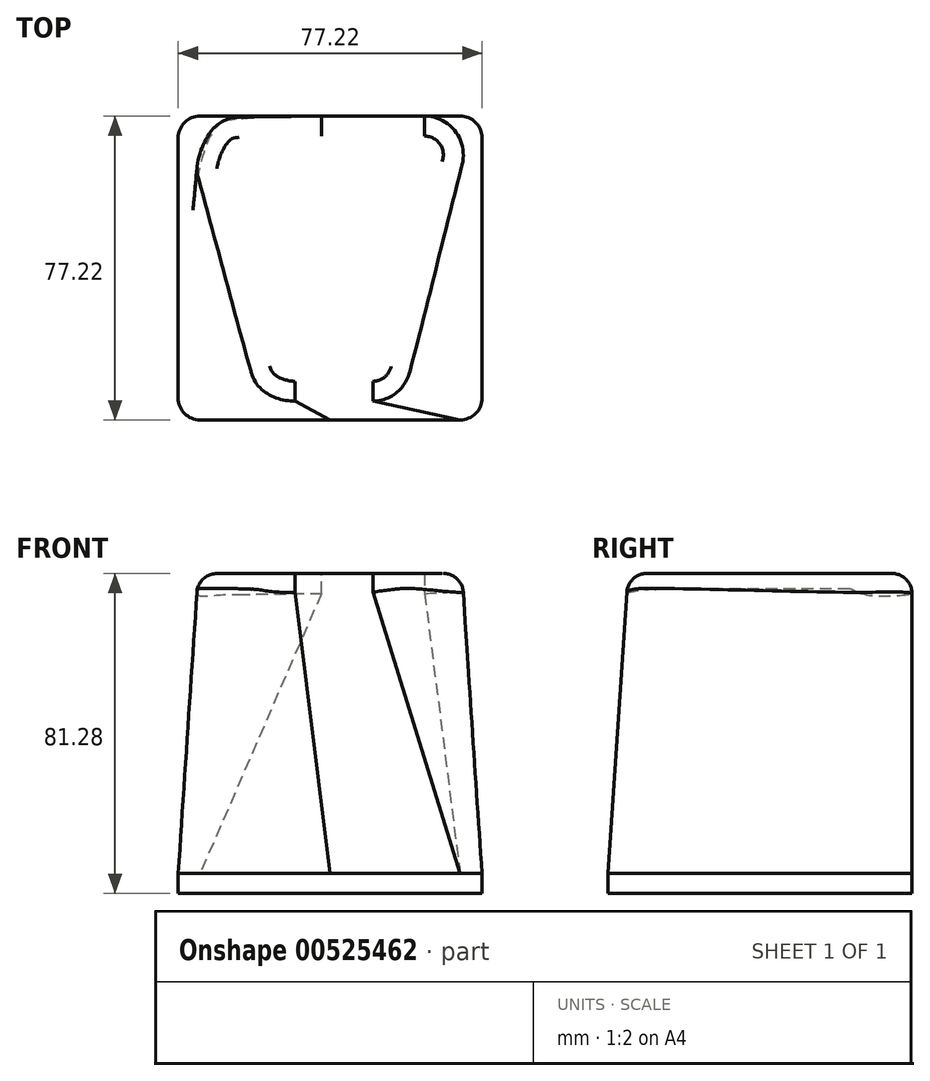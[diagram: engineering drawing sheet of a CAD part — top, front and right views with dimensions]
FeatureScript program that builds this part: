
annotation { "Feature Type Name" : "Feature", "Feature Type Description" : "" }
export const myFeature = defineFeature(function(context is Context, id is Id, definition is map)
    precondition{}
    {
        {
            var Q0;
            Q0=qCreatedBy(makeId("Top.planeOp"),FACE);
            var sketch = newSketch(context, id + "F0", { "sketchPlane" : qUnion([Q0])});
            skLineSegment(sketch, "E0.bottom", {"start": v(33.02, 38.1) * mm, "end": v(-33.02, 38.1) * mm, "construction": true});
            skLineSegment(sketch, "E0.top", {"start": v(33.02, -38.1) * mm, "end": v(-33.02, -38.1) * mm, "construction": true});
            skLineSegment(sketch, "E0.left", {"start": v(38.1, 33.02) * mm, "end": v(38.1, -33.02) * mm, "construction": true});
            skLineSegment(sketch, "E0.right", {"start": v(-38.1, 33.02) * mm, "end": v(-38.1, -33.02) * mm, "construction": true});
            skPoint(sketch, "E0.middle", {"position": v(0, 0) * mm});
            skPoint(sketch, "E1.visualSharp", {"position": v(-38.1, 38.1) * mm});
            skArc(sketch, "E1.filletArc", {"start": v(-33.02, 38.1) * mm, "mid": v(-36.61, 36.61) * mm, "end": v(-38.1, 33.02) * mm, "construction": true});
            skPoint(sketch, "E2.visualSharp", {"position": v(38.1, 38.1) * mm});
            skArc(sketch, "E2.filletArc", {"start": v(38.1, 33.02) * mm, "mid": v(36.61, 36.61) * mm, "end": v(33.02, 38.1) * mm, "construction": true});
            skPoint(sketch, "E3.visualSharp", {"position": v(38.1, -38.1) * mm});
            skArc(sketch, "E3.filletArc", {"start": v(33.02, -38.1) * mm, "mid": v(36.61, -36.61) * mm, "end": v(38.1, -33.02) * mm, "construction": true});
            skPoint(sketch, "E4.visualSharp", {"position": v(-38.1, -38.1) * mm});
            skArc(sketch, "E4.filletArc", {"start": v(-38.1, -33.02) * mm, "mid": v(-36.61, -36.61) * mm, "end": v(-33.02, -38.1) * mm, "construction": true});
            skLineSegment(sketch, "E5.0", {"start": v(-38.6, 33.02) * mm, "end": v(-38.6, -33.02) * mm});
            skArc(sketch, "E5.1", {"start": v(-33.02, 38.6) * mm, "mid": v(-36.97, 36.97) * mm, "end": v(-38.6, 33.02) * mm});
            skArc(sketch, "E5.2", {"start": v(-38.6, -33.02) * mm, "mid": v(-36.97, -36.97) * mm, "end": v(-33.02, -38.6) * mm});
            skLineSegment(sketch, "E5.3", {"start": v(33.02, 38.6) * mm, "end": v(-33.02, 38.6) * mm});
            skLineSegment(sketch, "E5.4", {"start": v(33.02, -38.6) * mm, "end": v(-33.02, -38.6) * mm});
            skArc(sketch, "E5.5", {"start": v(33.02, -38.6) * mm, "mid": v(36.97, -36.97) * mm, "end": v(38.6, -33.02) * mm});
            skLineSegment(sketch, "E5.6", {"start": v(38.6, 33.02) * mm, "end": v(38.6, -33.02) * mm});
            skArc(sketch, "E5.7", {"start": v(38.6, 33.02) * mm, "mid": v(36.97, 36.97) * mm, "end": v(33.02, 38.6) * mm});
            skSolve(sketch);
        }
        {
            var Q0;
            Q0=qCreatedBy(makeId("Top.planeOp"),FACE);
            cPlane(context, id + "F1", {"entities" : qUnion([Q0]), "cplaneType" : CPlaneType.OFFSET, "offset" : 76.2 * mm, "width" : 152.4 * mm, "height" : 152.4 * mm});
        }
        {
            var Q0;
            Q0=qCreatedBy(id+"F1.planeOp",FACE);
            var sketch = newSketch(context, id + "F2", { "sketchPlane" : qUnion([Q0])});
            skLineSegment(sketch, "E6", {"start": v(0, 38.6) * mm, "end": v(23.37, 38.6) * mm, "construction": true});
            skLineSegment(sketch, "E7", {"start": v(33.18, 25.82) * mm, "end": v(19.3, -26) * mm});
            skLineSegment(sketch, "E8", {"start": v(9.48, -33.53) * mm, "end": v(0, -33.53) * mm, "construction": true});
            skLineSegment(sketch, "E9", {"start": v(0, -33.53) * mm, "end": v(0, 38.6) * mm, "construction": true});
            skPoint(sketch, "E10.visualSharp", {"position": v(36.6, 38.6) * mm});
            skArc(sketch, "E10.filletArc", {"start": v(33.18, 25.82) * mm, "mid": v(31.43, 34.63) * mm, "end": v(23.37, 38.6) * mm});
            skPoint(sketch, "E11.visualSharp", {"position": v(17.28, -33.53) * mm});
            skArc(sketch, "E11.filletArc", {"start": v(9.48, -33.53) * mm, "mid": v(15.67, -31.43) * mm, "end": v(19.3, -26) * mm});
            skLineSegment(sketch, "E12.MirrorCS", {"start": v(0, 38.6) * mm, "end": v(-23.37, 38.6) * mm});
            skArc(sketch, "E13.MirrorCS", {"start": v(-33.18, 25.82) * mm, "mid": v(-31.43, 34.63) * mm, "end": v(-23.37, 38.6) * mm});
            skLineSegment(sketch, "E14.MirrorCS", {"start": v(-33.18, 25.82) * mm, "end": v(-19.3, -26) * mm});
            skArc(sketch, "E15.MirrorCS", {"start": v(-9.48, -33.53) * mm, "mid": v(-15.67, -31.43) * mm, "end": v(-19.3, -26) * mm});
            skLineSegment(sketch, "E16.MirrorCS", {"start": v(-9.48, -33.53) * mm, "end": v(0, -33.53) * mm, "construction": true});
            skLineSegment(sketch, "E17", {"start": v(-23.37, 38.6) * mm, "end": v(23.37, 38.6) * mm});
            skLineSegment(sketch, "E18", {"start": v(-9.48, -33.53) * mm, "end": v(9.48, -33.53) * mm});
            skSolve(sketch);
        }
        {
            var Q0;
            Q0=makeQuery(id+"F2.imprint","IMPRINT",FACE,{"disambiguationData":[TD([[makeQuery(id+"F2.imprint","IMPRINT",EDGE,{"derivedFrom":sQuery(id+"F2.wireOp",EDGE,"E7")}),-1.0]])]});
            var Q1;
            Q1=makeQuery(id+"F0.imprint","IMPRINT",FACE,{"disambiguationData":[TD([[makeQuery(id+"F0.imprint","IMPRINT",EDGE,{"derivedFrom":sQuery(id+"F0.wireOp",EDGE,"E5.0")}),1.0]])]});
            loft(context, id + "F3", {"sheetProfilesArray" : [{ "sheetProfileEntities" : qUnion([Q0]) }, { "sheetProfileEntities" : qUnion([Q1]) }]});
        }
        {
            var Q0;
            Q0=makeQuery(id+"F3.opLoft","MID_CAP_EDGE",EDGE,{"disambiguationData":[OSD([sQuery(id+"F2.wireOp",EDGE,"E14.MirrorCS"),sQuery(id+"F2.wireOp",EDGE,"E15.MirrorCS"),sQuery(id+"F2.wireOp",EDGE,"E18")])],"capPos":0.0});
            var Q1;
            Q1=makeQuery(id+"F3.opLoft","CAP_FACE",FACE,{"disambiguationData":[OSD([makeQuery(id+"F2.imprint","IMPRINT",FACE,{"disambiguationData":[TD([[makeQuery(id+"F2.imprint","IMPRINT",EDGE,{"derivedFrom":sQuery(id+"F2.wireOp",EDGE,"E7")}),-1.0]])]})])],"isStart":true});
            fillet(context, id + "F4", {"entities" : qUnion([Q0, Q1]), "radius" : 5.08 * mm, "tangentPropagation" : true, "allowEdgeOverflow" : false});
        }
        {
            var Q0;
            Q0=makeQuery(id+"F3.opLoft","CAP_FACE",FACE,{"disambiguationData":[OSD([makeQuery(id+"F0.imprint","IMPRINT",FACE,{"disambiguationData":[TD([[makeQuery(id+"F0.imprint","IMPRINT",EDGE,{"derivedFrom":sQuery(id+"F0.wireOp",EDGE,"E5.0")}),1.0]])]})])],"isStart":true});
            extrude(context, id + "F5", {"entities" : qUnion([Q0]), "operationType" : NewBodyOperationType.ADD, "depth" : 5.08 * mm, "offsetDistance" : 25.4 * mm});
        }
    });
